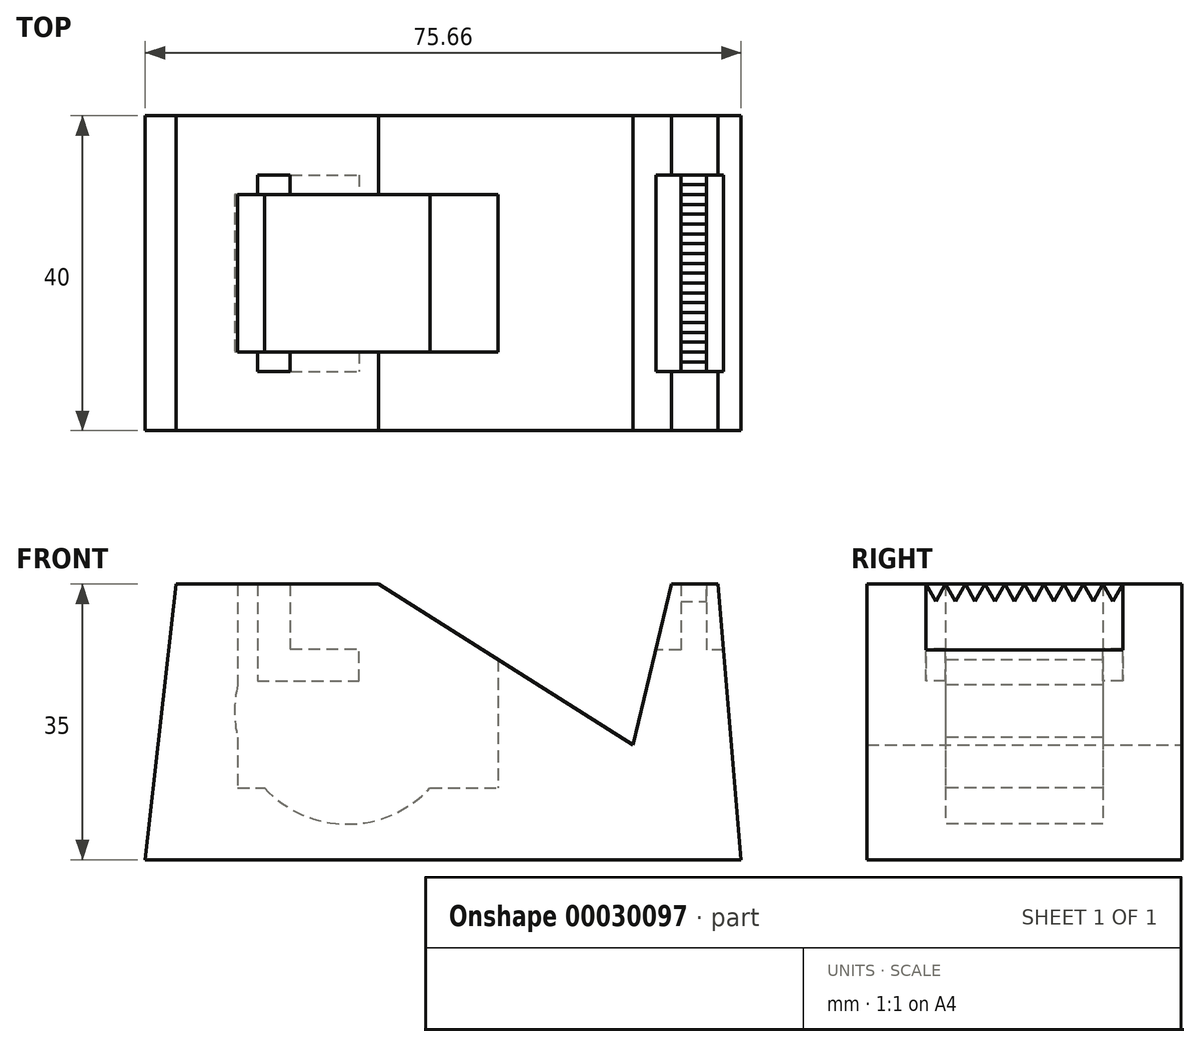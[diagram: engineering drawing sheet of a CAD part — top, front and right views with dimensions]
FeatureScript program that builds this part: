
annotation { "Feature Type Name" : "Feature", "Feature Type Description" : "" }
export const myFeature = defineFeature(function(context is Context, id is Id, definition is map)
    precondition{}
    {
        {
            var Q0;
            Q0=qCreatedBy(makeId("Front.planeOp"),FACE);
            var sketch = newSketch(context, id + "F0", { "sketchPlane" : qUnion([Q0])});
            skLineSegment(sketch, "E0", {"start": v(0, 0) * mm, "end": v(3.91, 35) * mm});
            skLineSegment(sketch, "E1", {"start": v(3.91, 35) * mm, "end": v(29.6, 35) * mm});
            skLineSegment(sketch, "E2", {"start": v(29.6, 35) * mm, "end": v(61.97, 14.56) * mm});
            skLineSegment(sketch, "E3", {"start": v(61.97, 14.56) * mm, "end": v(66.85, 35) * mm});
            skLineSegment(sketch, "E4", {"start": v(66.85, 35) * mm, "end": v(72.75, 35) * mm});
            skLineSegment(sketch, "E5", {"start": v(72.75, 35) * mm, "end": v(75.66, 0) * mm});
            skLineSegment(sketch, "E6", {"start": v(75.66, 0) * mm, "end": v(0, 0) * mm});
            skSolve(sketch);
        }
        {
            var Q0;
            Q0 = qSketchRegion(id + "F0", true);
            extrude(context, id + "F1", {"entities" : qUnion([Q0]), "endBound" : BoundingType.SYMMETRIC, "depth" : 40 * mm});
        }
        {
            var Q0;
            Q0=qCreatedBy(makeId("Front.planeOp"),FACE);
            var sketch = newSketch(context, id + "F2", { "sketchPlane" : qUnion([Q0])});
            skLineSegment(sketch, "E7.bottom", {"start": v(11.73, 40.7) * mm, "end": v(44.83, 40.7) * mm});
            skLineSegment(sketch, "E7.top", {"start": v(11.73, 9.1) * mm, "end": v(44.83, 9.1) * mm});
            skLineSegment(sketch, "E7.left", {"start": v(11.73, 40.7) * mm, "end": v(11.73, 9.1) * mm});
            skLineSegment(sketch, "E7.right", {"start": v(44.83, 40.7) * mm, "end": v(44.83, 9.1) * mm});
            skPoint(sketch, "E8.first.point", {"position": v(11.73, 27.16) * mm});
            skPoint(sketch, "E8.second.point", {"position": v(44.83, 21.14) * mm});
            skPoint(sketch, "E8.third.point", {"position": v(17.75, 9.1) * mm});
            skCircle(sketch, "E9", {"center": v(25.66, 18.85) * mm, "radius": 14.32 * mm});
            skSolve(sketch);
        }
        {
            var Q0;
            Q0 = qSketchRegion(id + "F2", true);
            extrude(context, id + "F3", {"entities" : qUnion([Q0]), "operationType" : NewBodyOperationType.REMOVE, "endBound" : BoundingType.SYMMETRIC, "oppositeDirection" : true, "depth" : 20 * mm});
        }
        {
            var Q0;
            Q0=qCreatedBy(makeId("Front.planeOp"),FACE);
            var sketch = newSketch(context, id + "F4", { "sketchPlane" : qUnion([Q0])});
            skLineSegment(sketch, "E10.bottom", {"start": v(14.24, 36.6) * mm, "end": v(18.4, 36.6) * mm});
            skLineSegment(sketch, "E10.top", {"start": v(14.24, 22.68) * mm, "end": v(18.4, 22.68) * mm});
            skLineSegment(sketch, "E10.left", {"start": v(14.24, 36.6) * mm, "end": v(14.24, 22.68) * mm});
            skLineSegment(sketch, "E10.right", {"start": v(18.4, 36.6) * mm, "end": v(18.4, 22.68) * mm});
            skLineSegment(sketch, "E11.bottom", {"start": v(14.24, 22.68) * mm, "end": v(27.12, 22.68) * mm});
            skLineSegment(sketch, "E11.top", {"start": v(14.24, 26.8) * mm, "end": v(27.12, 26.8) * mm});
            skLineSegment(sketch, "E11.left", {"start": v(14.24, 22.68) * mm, "end": v(14.24, 26.8) * mm});
            skLineSegment(sketch, "E11.right", {"start": v(27.12, 22.68) * mm, "end": v(27.12, 26.8) * mm});
            skSolve(sketch);
        }
        {
            var Q0;
            Q0 = qSketchRegion(id + "F4", true);
            extrude(context, id + "F5", {"entities" : qUnion([Q0]), "operationType" : NewBodyOperationType.REMOVE, "endBound" : BoundingType.SYMMETRIC, "oppositeDirection" : true, "depth" : 25 * mm});
        }
        {
            var Q0;
            Q0=qCreatedBy(makeId("Front.planeOp"),FACE);
            var sketch = newSketch(context, id + "F6", { "sketchPlane" : qUnion([Q0])});
            skLineSegment(sketch, "E12.bottom", {"start": v(82.7, 43.16) * mm, "end": v(71.27, 43.16) * mm});
            skLineSegment(sketch, "E12.top", {"start": v(82.7, 26.62) * mm, "end": v(71.27, 26.62) * mm});
            skLineSegment(sketch, "E12.left", {"start": v(82.7, 43.16) * mm, "end": v(82.7, 26.62) * mm});
            skLineSegment(sketch, "E12.right", {"start": v(71.27, 43.16) * mm, "end": v(71.27, 26.62) * mm});
            skPoint(sketch, "E13.oppositeSnap0", {"position": v(76.99, 26.62) * mm});
            skLineSegment(sketch, "E13.bottom", {"start": v(68.03, 43.16) * mm, "end": v(60.53, 43.16) * mm});
            skLineSegment(sketch, "E13.top", {"start": v(68.03, 26.62) * mm, "end": v(60.53, 26.62) * mm});
            skLineSegment(sketch, "E13.left", {"start": v(68.03, 43.16) * mm, "end": v(68.03, 26.62) * mm});
            skLineSegment(sketch, "E13.right", {"start": v(60.53, 43.16) * mm, "end": v(60.53, 26.62) * mm});
            skSolve(sketch);
        }
        {
            var Q0;
            Q0 = qSketchRegion(id + "F6", true);
            extrude(context, id + "F7", {"entities" : qUnion([Q0]), "operationType" : NewBodyOperationType.REMOVE, "endBound" : BoundingType.SYMMETRIC, "oppositeDirection" : true, "depth" : 25 * mm});
        }
        {
            var Q0;
            Q0=makeQuery(id+"F7.boolean.opBoolean","COPY",FACE,{"derivedFrom":makeQuery(id+"F7.opExtrude","SWEPT_FACE",FACE,{"disambiguationData":[OSD([sQuery(id+"F6.wireOp",EDGE,"E12.right")])]})});
            var sketch = newSketch(context, id + "F8", { "sketchPlane" : qUnion([Q0])});
            skLineSegment(sketch, "E14", {"start": v(-12.5, 35) * mm, "end": v(-11.25, 32.83) * mm});
            skLineSegment(sketch, "E15", {"start": v(-11.25, 32.83) * mm, "end": v(-10, 35) * mm});
            skLineSegment(sketch, "E16.1.0.0", {"start": v(-10, 35) * mm, "end": v(-8.75, 32.83) * mm});
            skLineSegment(sketch, "E16.1.0.1", {"start": v(-8.75, 32.83) * mm, "end": v(-7.5, 35) * mm});
            skLineSegment(sketch, "E16.2.0.0", {"start": v(-7.5, 35) * mm, "end": v(-6.25, 32.83) * mm});
            skLineSegment(sketch, "E16.2.0.1", {"start": v(-6.25, 32.83) * mm, "end": v(-5, 35) * mm});
            skLineSegment(sketch, "E16.3.0.0", {"start": v(-5, 35) * mm, "end": v(-3.75, 32.83) * mm});
            skLineSegment(sketch, "E16.3.0.1", {"start": v(-3.75, 32.83) * mm, "end": v(-2.5, 35) * mm});
            skLineSegment(sketch, "E16.4.0.0", {"start": v(-2.5, 35) * mm, "end": v(-1.25, 32.83) * mm});
            skLineSegment(sketch, "E16.4.0.1", {"start": v(-1.25, 32.83) * mm, "end": v(0, 35) * mm});
            skLineSegment(sketch, "E16.5.0.0", {"start": v(0, 35) * mm, "end": v(1.25, 32.83) * mm});
            skLineSegment(sketch, "E16.5.0.1", {"start": v(1.25, 32.83) * mm, "end": v(2.5, 35) * mm});
            skLineSegment(sketch, "E16.6.0.0", {"start": v(2.5, 35) * mm, "end": v(3.75, 32.83) * mm});
            skLineSegment(sketch, "E16.6.0.1", {"start": v(3.75, 32.83) * mm, "end": v(5, 35) * mm});
            skLineSegment(sketch, "E16.7.0.0", {"start": v(5, 35) * mm, "end": v(6.25, 32.83) * mm});
            skLineSegment(sketch, "E16.7.0.1", {"start": v(6.25, 32.83) * mm, "end": v(7.5, 35) * mm});
            skLineSegment(sketch, "E16.8.0.0", {"start": v(7.5, 35) * mm, "end": v(8.75, 32.83) * mm});
            skLineSegment(sketch, "E16.8.0.1", {"start": v(8.75, 32.83) * mm, "end": v(10, 35) * mm});
            skLineSegment(sketch, "E16.9.0.0", {"start": v(10, 35) * mm, "end": v(11.25, 32.83) * mm});
            skLineSegment(sketch, "E16.9.0.1", {"start": v(11.25, 32.83) * mm, "end": v(12.5, 35) * mm});
            skLineSegment(sketch, "E16.direction1", {"start": v(-11.25, 32.83) * mm, "end": v(-8.75, 32.83) * mm, "construction": true});
            skLineSegment(sketch, "E17", {"start": v(12.5, 35) * mm, "end": v(12.5, 38.02) * mm});
            skLineSegment(sketch, "E18", {"start": v(12.5, 38.02) * mm, "end": v(-12.5, 38.02) * mm});
            skLineSegment(sketch, "E19", {"start": v(-12.5, 38.02) * mm, "end": v(-12.5, 35) * mm});
            skSolve(sketch);
        }
        {
            var Q0;
            Q0 = qSketchRegion(id + "F8", true);
            extrude(context, id + "F9", {"entities" : qUnion([Q0]), "operationType" : NewBodyOperationType.REMOVE, "oppositeDirection" : true, "depth" : 10 * mm});
        }
    });
